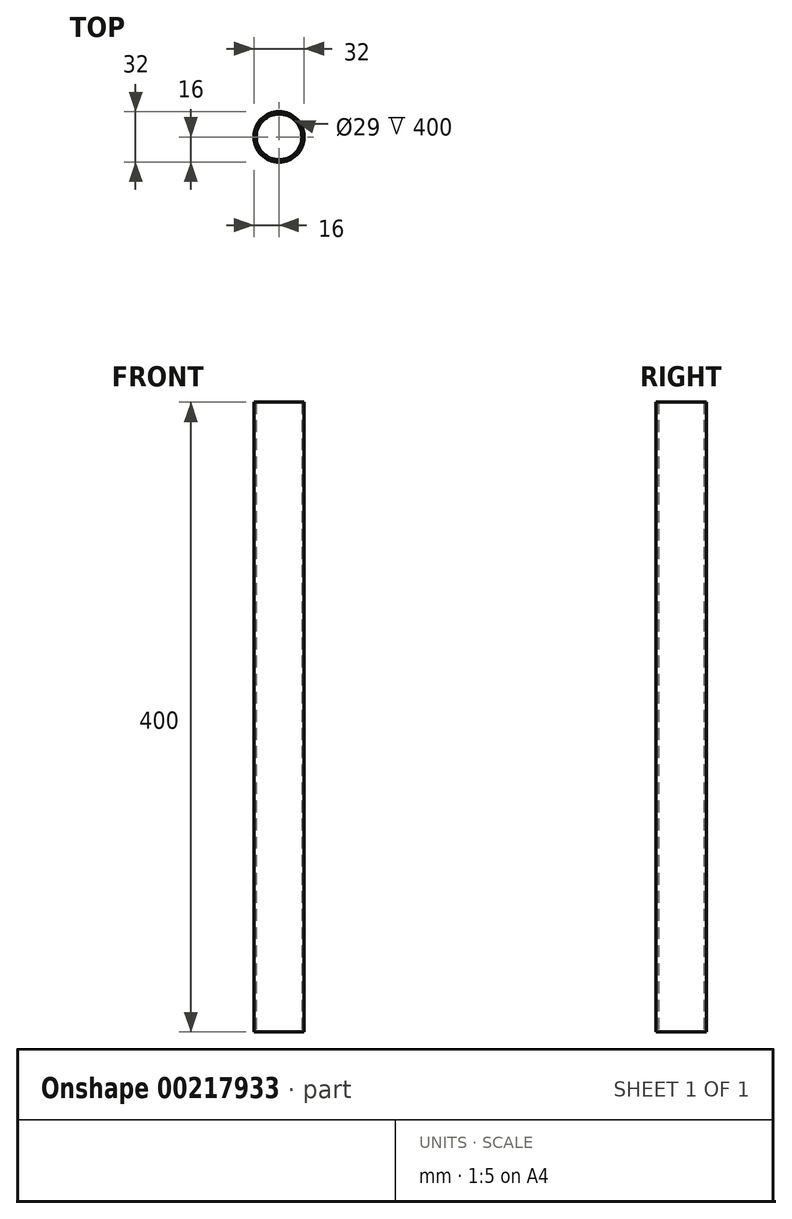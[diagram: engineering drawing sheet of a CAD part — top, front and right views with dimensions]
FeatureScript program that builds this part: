
annotation { "Feature Type Name" : "Feature", "Feature Type Description" : "" }
export const myFeature = defineFeature(function(context is Context, id is Id, definition is map)
    precondition{}
    {
        {
            var Q0;
            Q0=qCreatedBy(makeId("Top.planeOp"),FACE);
            var sketch = newSketch(context, id + "F0", { "sketchPlane" : qUnion([Q0])});
            skCircle(sketch, "E0", {"center": v(0, 0) * mm, "radius": 16 * mm});
            skCircle(sketch, "E1", {"center": v(0, 0) * mm, "radius": 14.5 * mm});
            skSolve(sketch);
        }
        {
            var Q0;
            Q0=makeQuery(id+"F0.imprint","IMPRINT",FACE,{"disambiguationData":[TD([[makeQuery(id+"F0.imprint","IMPRINT",EDGE,{"derivedFrom":sQuery(id+"F0.wireOp",EDGE,"E0")}),1.0]])]});
            extrude(context, id + "F1", {"entities" : qUnion([Q0]), "depth" : 400 * mm});
        }
    });
